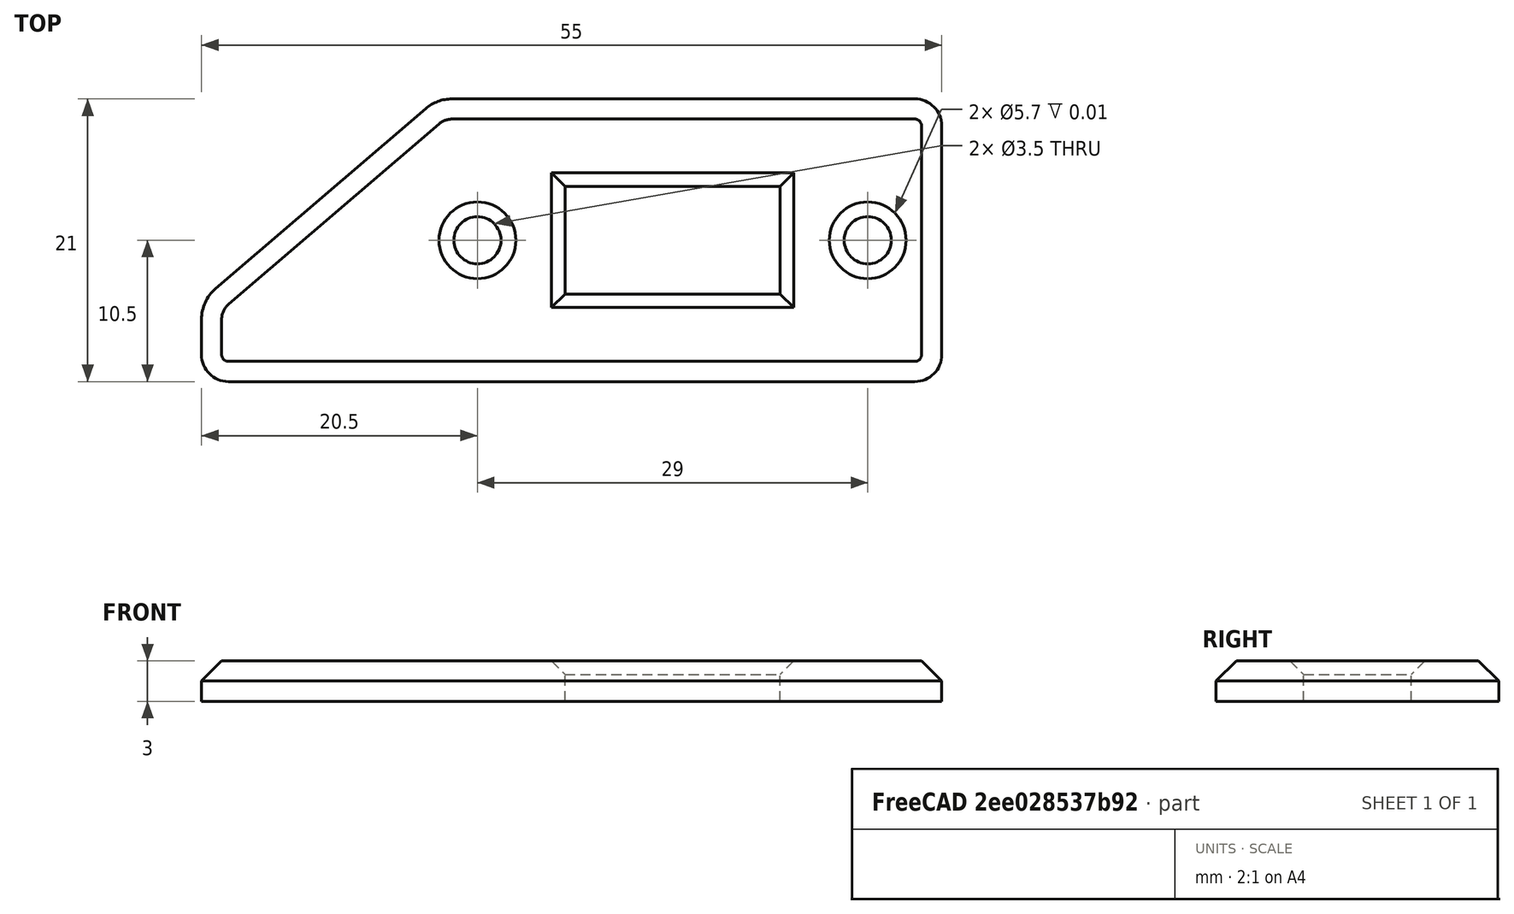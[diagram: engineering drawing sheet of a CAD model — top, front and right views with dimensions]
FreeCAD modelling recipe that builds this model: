
FCSTD DOCUMENT  (FreeCAD 0.19R)
Label: USBBezel
License: All rights reserved
LicenseURL: http://en.wikipedia.org/wiki/All_rights_reserved
objects: Sketcher::SketchObject×3, PartDesign::Pocket×2, PartDesign::Fillet×2, PartDesign::Chamfer×2, PartDesign::Pad×1, PartDesign::Body×1, Mesh::Feature×1
note: 18 computed .brp shape members not serialized (recipe doc carries the construction recipe); baked Part::Feature solids carry a one-line shape summary decoded from their .brp

FEATURE [Sketcher::SketchObject] Sketch
  FullyConstrained = true
  MapMode = 5
  Support = -> [XY_Plane]
  sketch-geometry (9):
    g0: LineSegment StartX=-8 StartY=4 StartZ=0 EndX=8 EndY=4 EndZ=0
    g1: LineSegment StartX=8 StartY=4 StartZ=0 EndX=8 EndY=-4 EndZ=0
    g2: LineSegment StartX=8 StartY=-4 StartZ=0 EndX=-8 EndY=-4 EndZ=0
    g3: LineSegment StartX=-8 StartY=-4 StartZ=0 EndX=-8 EndY=4 EndZ=0
    g4: LineSegment StartX=20 StartY=-10.5 StartZ=0 EndX=20 EndY=10.5 EndZ=0
    g5: LineSegment StartX=20 StartY=10.5 StartZ=0 EndX=-17.5 EndY=10.5 EndZ=0
    g6: LineSegment StartX=-17.5 StartY=10.5 StartZ=0 EndX=-35 EndY=-4.5 EndZ=0
    g7: LineSegment StartX=-35 StartY=-4.5 StartZ=0 EndX=-35 EndY=-10.5 EndZ=0
    g8: LineSegment StartX=-35 StartY=-10.5 StartZ=0 EndX=20 EndY=-10.5 EndZ=0
  constraints (26):
    c: Coincident(g0,g1)
    c: Coincident(g1,g2)
    c: Coincident(g2,g3)
    c: Coincident(g3,g0)
    c: Horizontal(g0)
    c: Horizontal(g2)
    c: Vertical(g1)
    c: Vertical(g3)
    c: Symmetric(g1,g0,g-1)
    c: Distance(g1) = 8
    c: Distance(g0) = 16
    c: Vertical(g4)
    c: Coincident(g4,g5)
    c: Horizontal(g5)
    c: Coincident(g5,g6)
    c: Coincident(g6,g7)
    c: Vertical(g7)
    c: Coincident(g7,g8)
    c: Coincident(g8,g4)
    c: Horizontal(g8)
    c: DistanceX(g7) = -35
    c: Distance(g7) = 6
    c: Distance(g0,g5) = 6.5
    c: Distance(g1,g8) = 6.5
    c: Distance(g1,g4) = 12
    c: DistanceX(g5) = -17.5
FEATURE [PartDesign::Pad] Pad
  Direction = (1,1,1)
  Length = 3
  Length2 = 100
  Profile = -> Sketch
  Type = 0
FEATURE [Sketcher::SketchObject] Sketch001
  FullyConstrained = true
  MapMode = 5
  Placement = pos=(0,0,3) rot=(0,0,1;0rad)
  Support = -> [Pad]
  sketch-geometry (2):
    g0: Circle CenterX=-14.5 CenterY=0 CenterZ=0 NormalX=0 NormalY=0 NormalZ=1 AngleXU=0 Radius=2.85
    g1: Circle CenterX=14.5 CenterY=0 CenterZ=0 NormalX=0 NormalY=0 NormalZ=1 AngleXU=0 Radius=2.85
  constraints (5):
    c: Symmetric(g0,g1,g-1)
    c: PointOnObject(g1,g-1)
    c: Distance(g1,g0) = 29
    c: Diameter(g1) = 5.7
    c: Diameter(g0) = 5.7
FEATURE [PartDesign::Pocket] Pocket
  BaseFeature = -> Pad
  Length = 0.01
  Length2 = 100
  Profile = -> Sketch001
  Type = 0
FEATURE [Sketcher::SketchObject] Sketch002
  ExternalGeometry = -> [Pocket]
  FullyConstrained = true
  MapMode = 5
  Placement = pos=(0,0,2.99) rot=(0,0,1;0rad)
  Support = -> [Pocket]
  sketch-geometry (2):
    g0: Circle CenterX=-14.5 CenterY=0 CenterZ=0 NormalX=0 NormalY=0 NormalZ=1 AngleXU=0 Radius=1.75
    g1: Circle CenterX=14.5 CenterY=0 CenterZ=0 NormalX=0 NormalY=0 NormalZ=1 AngleXU=0 Radius=1.75
  constraints (4):
    c: Coincident(g-4,g1)
    c: Coincident(g-3,g0)
    c: Diameter(g0) = 3.5
    c: Equal(g0,g1)
FEATURE [PartDesign::Pocket] Pocket001
  BaseFeature = -> Pocket
  Length = 5
  Length2 = 100
  Profile = -> Sketch002
  Type = 0
FEATURE [PartDesign::Fillet] Fillet
  Base = -> Pocket001 [Edge1,Edge2,Edge5]
  BaseFeature = -> Pocket001
  Radius = 2
  SupportTransform = false
FEATURE [PartDesign::Fillet] Fillet001
  Base = -> Fillet [Edge36,Edge34]
  BaseFeature = -> Fillet
  Radius = 3
  SupportTransform = false
FEATURE [PartDesign::Chamfer] Chamfer
  Angle = 45
  Base = -> Fillet001 [Edge35]
  BaseFeature = -> Fillet001
  ChamferType = 0
  FlipDirection = false
  Size = 1.5
  Size2 = 1
  SupportTransform = false
FEATURE [PartDesign::Chamfer] Chamfer001
  Angle = 45
  Base = -> Chamfer [Edge41,Edge43,Edge44,Edge42]
  BaseFeature = -> Chamfer
  ChamferType = 0
  FlipDirection = false
  Size = 1
  Size2 = 1
  SupportTransform = false
FEATURE [PartDesign::Body] Body
  Group = -> [Sketch,Pad,Sketch001,Pocket,Sketch002,Pocket001,Fillet,Fillet001,Chamfer,Chamfer001]
  Origin = -> Origin
  Tip = -> Chamfer001
FEATURE [Mesh::Feature] Mesh  label="Chamfer002 (Meshed)"
